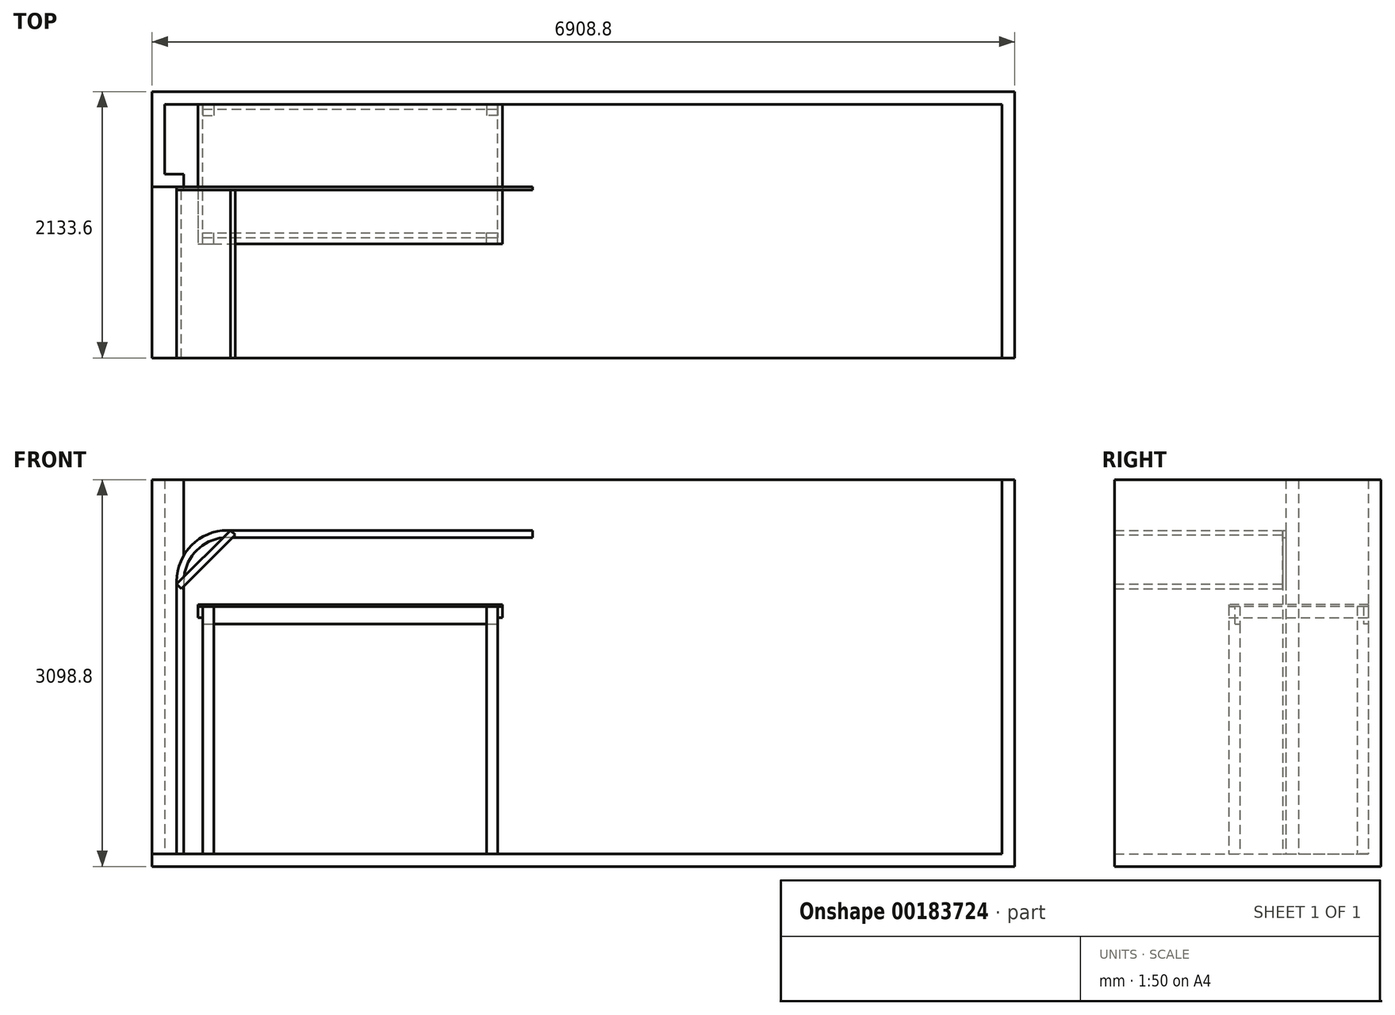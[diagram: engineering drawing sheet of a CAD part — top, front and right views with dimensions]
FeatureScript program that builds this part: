
annotation { "Feature Type Name" : "Feature", "Feature Type Description" : "" }
export const myFeature = defineFeature(function(context is Context, id is Id, definition is map)
    precondition{}
    {
        {
            var Q0;
            Q0=qCreatedBy(makeId("Top.planeOp"),FACE);
            var sketch = newSketch(context, id + "F0", { "sketchPlane" : qUnion([Q0])});
            skLineSegment(sketch, "E0", {"start": v(0, 0) * mm, "end": v(-152.4, 0) * mm});
            skLineSegment(sketch, "E1", {"start": v(-152.4, 0) * mm, "end": v(-152.4, 558.8) * mm});
            skLineSegment(sketch, "E2", {"start": v(-152.4, 558.8) * mm, "end": v(6553.2, 558.8) * mm});
            skLineSegment(sketch, "E3", {"start": v(6553.2, 558.8) * mm, "end": v(6553.2, 660.4) * mm, "construction": true});
            skLineSegment(sketch, "E4", {"start": v(6553.2, 660.4) * mm, "end": v(-254, 660.4) * mm});
            skLineSegment(sketch, "E5", {"start": v(-254, 660.4) * mm, "end": v(-254, -101.6) * mm});
            skLineSegment(sketch, "E6", {"start": v(-254, -101.6) * mm, "end": v(0, -101.6) * mm});
            skLineSegment(sketch, "E7", {"start": v(0, -101.6) * mm, "end": v(0, 0) * mm});
            skLineSegment(sketch, "E8", {"start": v(-152.4, 558.8) * mm, "end": v(-152.4, 660.4) * mm, "construction": true});
            skLineSegment(sketch, "E9", {"start": v(-152.4, 558.8) * mm, "end": v(-254, 558.8) * mm, "construction": true});
            skLineSegment(sketch, "E10", {"start": v(6553.2, 660.4) * mm, "end": v(6654.8, 660.4) * mm});
            skLineSegment(sketch, "E11", {"start": v(6654.8, 660.4) * mm, "end": v(6654.8, -1473.2) * mm});
            skLineSegment(sketch, "E12", {"start": v(6654.8, -1473.2) * mm, "end": v(6553.2, -1473.2) * mm});
            skLineSegment(sketch, "E13", {"start": v(6553.2, -1473.2) * mm, "end": v(6553.2, 558.8) * mm});
            skSolve(sketch);
        }
        {
            var Q0;
            Q0 = qSketchRegion(id + "F0", true);
            extrude(context, id + "F1", {"entities" : qUnion([Q0]), "depth" : 2997.2 * mm});
        }
        {
            var Q0;
            Q0=makeQuery(id+"F1.opExtrude","CAP_FACE",FACE,{"disambiguationData":[OSD([sQuery(id+"F0.wireOp",EDGE,"E0"),sQuery(id+"F0.wireOp",EDGE,"E1"),sQuery(id+"F0.wireOp",EDGE,"E2"),sQuery(id+"F0.wireOp",EDGE,"E4"),sQuery(id+"F0.wireOp",EDGE,"E5"),sQuery(id+"F0.wireOp",EDGE,"E6"),sQuery(id+"F0.wireOp",EDGE,"E7"),sQuery(id+"F0.wireOp",EDGE,"E10"),sQuery(id+"F0.wireOp",EDGE,"E11"),sQuery(id+"F0.wireOp",EDGE,"E12"),sQuery(id+"F0.wireOp",EDGE,"E13")])],"isStart":true});
            var sketch = newSketch(context, id + "F2", { "sketchPlane" : qUnion([Q0])});
            skLineSegment(sketch, "E14.bottom", {"start": v(6654.8, 1473.2) * mm, "end": v(-254, 1473.2) * mm});
            skLineSegment(sketch, "E14.top", {"start": v(6654.8, -660.4) * mm, "end": v(-254, -660.4) * mm});
            skLineSegment(sketch, "E14.left", {"start": v(6654.8, 1473.2) * mm, "end": v(6654.8, -660.4) * mm});
            skLineSegment(sketch, "E14.right", {"start": v(-254, 1473.2) * mm, "end": v(-254, -660.4) * mm});
            skSolve(sketch);
        }
        {
            var Q0;
            Q0 = qSketchRegion(id + "F2", true);
            extrude(context, id + "F3", {"entities" : qUnion([Q0]), "operationType" : NewBodyOperationType.ADD, "depth" : 101.6 * mm});
        }
        {
            var Q0;
            Q0=makeQuery(id+"F1.opExtrude","SWEPT_FACE",FACE,{"disambiguationData":[OSD([sQuery(id+"F0.wireOp",EDGE,"E6")])]});
            var sketch = newSketch(context, id + "F4", { "sketchPlane" : qUnion([Q0])});
            skArc(sketch, "E15", {"start": v(349.25, 2590.8) * mm, "mid": v(61.88, 2471.77) * mm, "end": v(-57.15, 2184.4) * mm});
            skLineSegment(sketch, "E16", {"start": v(-57.15, 2184.4) * mm, "end": v(-57.15, 0) * mm});
            skLineSegment(sketch, "E17", {"start": v(349.25, 2590.8) * mm, "end": v(2794, 2590.8) * mm});
            skLineSegment(sketch, "E18", {"start": v(2794, 2590.8) * mm, "end": v(2794, 2533.65) * mm});
            skLineSegment(sketch, "E19", {"start": v(2794, 2533.65) * mm, "end": v(349.25, 2533.65) * mm});
            skLineSegment(sketch, "E20", {"start": v(-57.15, 0) * mm, "end": v(0, 0) * mm});
            skLineSegment(sketch, "E21", {"start": v(0, 0) * mm, "end": v(0, 2184.4) * mm});
            skArc(sketch, "E22", {"start": v(349.25, 2533.65) * mm, "mid": v(102.3, 2431.36) * mm, "end": v(0, 2184.4) * mm});
            skLineSegment(sketch, "E23", {"start": v(349.25, 2590.8) * mm, "end": v(349.25, 2533.65) * mm, "construction": true});
            skLineSegment(sketch, "E24", {"start": v(0, 2184.4) * mm, "end": v(-57.15, 2184.4) * mm, "construction": true});
            skSolve(sketch);
        }
        {
            var Q0;
            Q0 = qSketchRegion(id + "F4", true);
            extrude(context, id + "F5", {"entities" : qUnion([Q0]), "depth" : 25.4 * mm});
        }
        {
            var Q0;
            Q0=makeQuery(id+"F5.opExtrude","CAP_FACE",FACE,{"disambiguationData":[OSD([sQuery(id+"F4.wireOp",EDGE,"E15"),sQuery(id+"F4.wireOp",EDGE,"E16"),sQuery(id+"F4.wireOp",EDGE,"E17"),sQuery(id+"F4.wireOp",EDGE,"E18"),sQuery(id+"F4.wireOp",EDGE,"E19"),sQuery(id+"F4.wireOp",EDGE,"E20"),sQuery(id+"F4.wireOp",EDGE,"E21"),sQuery(id+"F4.wireOp",EDGE,"E22")])],"isStart":false});
            var sketch = newSketch(context, id + "F6", { "sketchPlane" : qUnion([Q0])});
            skLineSegment(sketch, "E25", {"start": v(-57.15, 2159.75) * mm, "end": v(373.9, 2590.8) * mm});
            skLineSegment(sketch, "E26", {"start": v(373.9, 2590.8) * mm, "end": v(409.82, 2554.88) * mm});
            skLineSegment(sketch, "E27", {"start": v(409.82, 2554.88) * mm, "end": v(-21.23, 2123.83) * mm});
            skLineSegment(sketch, "E28", {"start": v(-21.23, 2123.83) * mm, "end": v(-57.15, 2159.75) * mm});
            skSolve(sketch);
        }
        {
            var Q0;
            Q0 = qSketchRegion(id + "F6", true);
            var Q1;
            Q1=makeQuery(id+"F3.boolean.opBoolean","MERGE",FACE,{"derivedFrom":[makeQuery(id+"F1.opExtrude","SWEPT_FACE",FACE,{"disambiguationData":[OSD([sQuery(id+"F0.wireOp",EDGE,"E12")])]}),makeQuery(id+"F3.opExtrude","SWEPT_FACE",FACE,{"disambiguationData":[OSD([sQuery(id+"F2.wireOp",EDGE,"E14.bottom")])]})]});
            extrude(context, id + "F7", {"entities" : qUnion([Q0]), "endBound" : BoundingType.UP_TO_SURFACE, "endBoundEntityFace" : qUnion([Q1]), "depth" : 2433.32 * mm});
        }
        {
            var Q0;
            Q0=makeQuery(id+"F3.opExtrude","CAP_FACE",FACE,{"disambiguationData":[OSD([sQuery(id+"F2.wireOp",EDGE,"E14.bottom"),sQuery(id+"F2.wireOp",EDGE,"E14.top"),sQuery(id+"F2.wireOp",EDGE,"E14.left"),sQuery(id+"F2.wireOp",EDGE,"E14.right")])],"isStart":true});
            var sketch = newSketch(context, id + "F8", { "sketchPlane" : qUnion([Q0])});
            skLineSegment(sketch, "E29.bottom", {"start": v(152.4, 558.8) * mm, "end": v(241.3, 558.8) * mm});
            skLineSegment(sketch, "E29.top", {"start": v(152.4, 469.9) * mm, "end": v(241.3, 469.9) * mm});
            skLineSegment(sketch, "E29.left", {"start": v(152.4, 558.8) * mm, "end": v(152.4, 469.9) * mm});
            skLineSegment(sketch, "E29.right", {"start": v(241.3, 558.8) * mm, "end": v(241.3, 469.9) * mm});
            skLineSegment(sketch, "E30", {"start": v(241.3, 469.9) * mm, "end": v(2425.7, 469.9) * mm, "construction": true});
            skLineSegment(sketch, "E31", {"start": v(1333.5, 469.9) * mm, "end": v(1333.5, -469.9) * mm, "construction": true});
            skLineSegment(sketch, "E32", {"start": v(1333.5, -469.9) * mm, "end": v(241.3, -469.9) * mm, "construction": true});
            skLineSegment(sketch, "E33.MirrorCS", {"start": v(2425.7, 558.8) * mm, "end": v(2425.7, 469.9) * mm});
            skLineSegment(sketch, "E34.MirrorCS", {"start": v(2514.6, 558.8) * mm, "end": v(2425.7, 558.8) * mm});
            skLineSegment(sketch, "E35.MirrorCS", {"start": v(2514.6, 558.8) * mm, "end": v(2514.6, 469.9) * mm});
            skLineSegment(sketch, "E36.MirrorCS", {"start": v(2514.6, 469.9) * mm, "end": v(2425.7, 469.9) * mm});
            skLineSegment(sketch, "E37.MirrorCS", {"start": v(1333.5, -469.9) * mm, "end": v(2425.7, -469.9) * mm, "construction": true});
            skLineSegment(sketch, "E38", {"start": v(1333.5, 0) * mm, "end": v(241.3, 0) * mm, "construction": true});
            skLineSegment(sketch, "E39", {"start": v(241.3, 0) * mm, "end": v(241.3, 469.9) * mm, "construction": true});
            skLineSegment(sketch, "E40.MirrorCS", {"start": v(152.4, -558.8) * mm, "end": v(152.4, -469.9) * mm});
            skLineSegment(sketch, "E41.MirrorCS", {"start": v(152.4, -558.8) * mm, "end": v(241.3, -558.8) * mm});
            skLineSegment(sketch, "E42.MirrorCS", {"start": v(241.3, -558.8) * mm, "end": v(241.3, -469.9) * mm});
            skLineSegment(sketch, "E43.MirrorCS", {"start": v(152.4, -469.9) * mm, "end": v(241.3, -469.9) * mm});
            skLineSegment(sketch, "E44.MirrorCS", {"start": v(2425.7, -558.8) * mm, "end": v(2425.7, -469.9) * mm});
            skLineSegment(sketch, "E45.MirrorCS", {"start": v(2514.6, -558.8) * mm, "end": v(2425.7, -558.8) * mm});
            skLineSegment(sketch, "E46.MirrorCS", {"start": v(2514.6, -469.9) * mm, "end": v(2425.7, -469.9) * mm});
            skLineSegment(sketch, "E47.MirrorCS", {"start": v(2514.6, -558.8) * mm, "end": v(2514.6, -469.9) * mm});
            skSolve(sketch);
        }
        {
            var Q0;
            Q0 = qSketchRegion(id + "F8", true);
            extrude(context, id + "F9", {"entities" : qUnion([Q0]), "depth" : 1981.2 * mm});
        }
        {
            var Q0;
            Q0=makeQuery(id+"F9.opExtrude","SWEPT_FACE",FACE,{"disambiguationData":[OSD([sQuery(id+"F8.wireOp",EDGE,"E35.MirrorCS")])]});
            var sketch = newSketch(context, id + "F10", { "sketchPlane" : qUnion([Q0])});
            skLineSegment(sketch, "E48.bottom", {"start": v(558.8, 1981.2) * mm, "end": v(520.7, 1981.2) * mm});
            skLineSegment(sketch, "E48.top", {"start": v(558.8, 1841.5) * mm, "end": v(520.7, 1841.5) * mm});
            skLineSegment(sketch, "E48.left", {"start": v(558.8, 1981.2) * mm, "end": v(558.8, 1841.5) * mm});
            skLineSegment(sketch, "E48.right", {"start": v(520.7, 1981.2) * mm, "end": v(520.7, 1841.5) * mm});
            skPoint(sketch, "E49.0", {"position": v(-514.35, 1981.2) * mm});
            skPoint(sketch, "E50.0", {"position": v(-469.9, 1981.2) * mm});
            skLineSegment(sketch, "E51.0", {"start": v(-469.9, 1981.2) * mm, "end": v(-469.9, 0) * mm, "construction": true});
            skLineSegment(sketch, "E52.0", {"start": v(-558.8, 1981.2) * mm, "end": v(-469.9, 1981.2) * mm, "construction": true});
            skLineSegment(sketch, "E53.bottom", {"start": v(-469.9, 1981.2) * mm, "end": v(-508, 1981.2) * mm});
            skLineSegment(sketch, "E53.top", {"start": v(-469.9, 1841.5) * mm, "end": v(-508, 1841.5) * mm});
            skLineSegment(sketch, "E53.left", {"start": v(-469.9, 1981.2) * mm, "end": v(-469.9, 1841.5) * mm});
            skLineSegment(sketch, "E53.right", {"start": v(-508, 1981.2) * mm, "end": v(-508, 1841.5) * mm});
            skSolve(sketch);
        }
        {
            var Q0;
            Q0 = qSketchRegion(id + "F10", true);
            var Q1;
            Q1=makeQuery(id+"F1.opExtrude","SWEPT_FACE",FACE,{"disambiguationData":[OSD([sQuery(id+"F0.wireOp",EDGE,"E1")])]});
            extrude(context, id + "F11", {"entities" : qUnion([Q0]), "operationType" : NewBodyOperationType.REMOVE, "endBound" : BoundingType.UP_TO_SURFACE, "oppositeDirection" : true, "endBoundEntityFace" : qUnion([Q1]), "depth" : 25.4 * mm});
        }
        {
            var Q0;
            Q0 = qSketchRegion(id + "F10", true);
            var Q1;
            Q1=makeQuery(id+"F9.opExtrude","SWEPT_FACE",FACE,{"disambiguationData":[OSD([sQuery(id+"F8.wireOp",EDGE,"E40.MirrorCS")])]});
            extrude(context, id + "F12", {"entities" : qUnion([Q0]), "endBound" : BoundingType.UP_TO_SURFACE, "oppositeDirection" : true, "endBoundEntityFace" : qUnion([Q1]), "depth" : 1790.7 * mm});
        }
        {
            var Q0;
            Q0=makeQuery(id+"F9.opExtrude","SWEPT_FACE",FACE,{"disambiguationData":[OSD([sQuery(id+"F8.wireOp",EDGE,"E47.MirrorCS")])]});
            var Q1;
            Q1=makeQuery(id+"F9.opExtrude","SWEPT_FACE",FACE,{"disambiguationData":[OSD([sQuery(id+"F8.wireOp",EDGE,"E40.MirrorCS")])]});
            cPlane(context, id + "F13", {"entities" : qUnion([Q0, Q1]), "cplaneType" : CPlaneType.MID_PLANE, "offset" : 25.4 * mm, "width" : 152.4 * mm, "height" : 152.4 * mm});
        }
        {
            var Q0;
            Q0=makeQuery(id+"F9.opExtrude","SWEPT_FACE",FACE,{"disambiguationData":[OSD([sQuery(id+"F8.wireOp",EDGE,"E47.MirrorCS")])]});
            var sketch = newSketch(context, id + "F14", { "sketchPlane" : qUnion([Q0])});
            skLineSegment(sketch, "E54.0", {"start": v(558.8, 1841.5) * mm, "end": v(558.8, 0) * mm, "construction": true});
            skPoint(sketch, "E55.0", {"position": v(558.8, 1981.2) * mm});
            skLineSegment(sketch, "E56.bottom", {"start": v(-558.8, 1981.2) * mm, "end": v(558.8, 1981.2) * mm});
            skLineSegment(sketch, "E56.top", {"start": v(-558.8, 1892.3) * mm, "end": v(558.8, 1892.3) * mm});
            skLineSegment(sketch, "E56.left", {"start": v(-558.8, 1981.2) * mm, "end": v(-558.8, 1892.3) * mm});
            skLineSegment(sketch, "E56.right", {"start": v(558.8, 1981.2) * mm, "end": v(558.8, 1892.3) * mm});
            skSolve(sketch);
        }
        {
            var Q0;
            Q0 = qSketchRegion(id + "F14", true);
            extrude(context, id + "F15", {"entities" : qUnion([Q0]), "depth" : 38.1 * mm});
        }
        {
            var Q0;
            Q0=makeQuery(id+"F15.opExtrude","SWEPT_BODY",BODY,{"disambiguationData":[OSD([sQuery(id+"F14.wireOp",EDGE,"E56.bottom"),sQuery(id+"F14.wireOp",EDGE,"E56.top"),sQuery(id+"F14.wireOp",EDGE,"E56.left"),sQuery(id+"F14.wireOp",EDGE,"E56.right")])]});
            var Q1;
            Q1=qCreatedBy(id+"F13.planeOp",FACE);
            mirror(context, id + "F16", {"entities" : qUnion([Q0]), "mirrorPlane" : qUnion([Q1])});
        }
        {
            var Q0;
            Q0=makeQuery(id+"F9.opExtrude","CAP_FACE",FACE,{"disambiguationData":[OSD([sQuery(id+"F8.wireOp",EDGE,"E29.bottom"),sQuery(id+"F8.wireOp",EDGE,"E29.top"),sQuery(id+"F8.wireOp",EDGE,"E29.left"),sQuery(id+"F8.wireOp",EDGE,"E29.right")])],"isStart":false});
            var sketch = newSketch(context, id + "F17", { "sketchPlane" : qUnion([Q0])});
            skPoint(sketch, "E57.0", {"position": v(114.3, 558.8) * mm});
            skPoint(sketch, "E58.0", {"position": v(2552.7, -558.8) * mm});
            skLineSegment(sketch, "E59.bottom", {"start": v(114.3, 558.8) * mm, "end": v(2552.7, 558.8) * mm});
            skLineSegment(sketch, "E59.top", {"start": v(114.3, -558.8) * mm, "end": v(2552.7, -558.8) * mm});
            skLineSegment(sketch, "E59.left", {"start": v(114.3, 558.8) * mm, "end": v(114.3, -558.8) * mm});
            skLineSegment(sketch, "E59.right", {"start": v(2552.7, 558.8) * mm, "end": v(2552.7, -558.8) * mm});
            skSolve(sketch);
        }
        {
            var Q0;
            Q0 = qSketchRegion(id + "F17", true);
            extrude(context, id + "F18", {"entities" : qUnion([Q0]), "depth" : 15.88 * mm});
        }
    });
